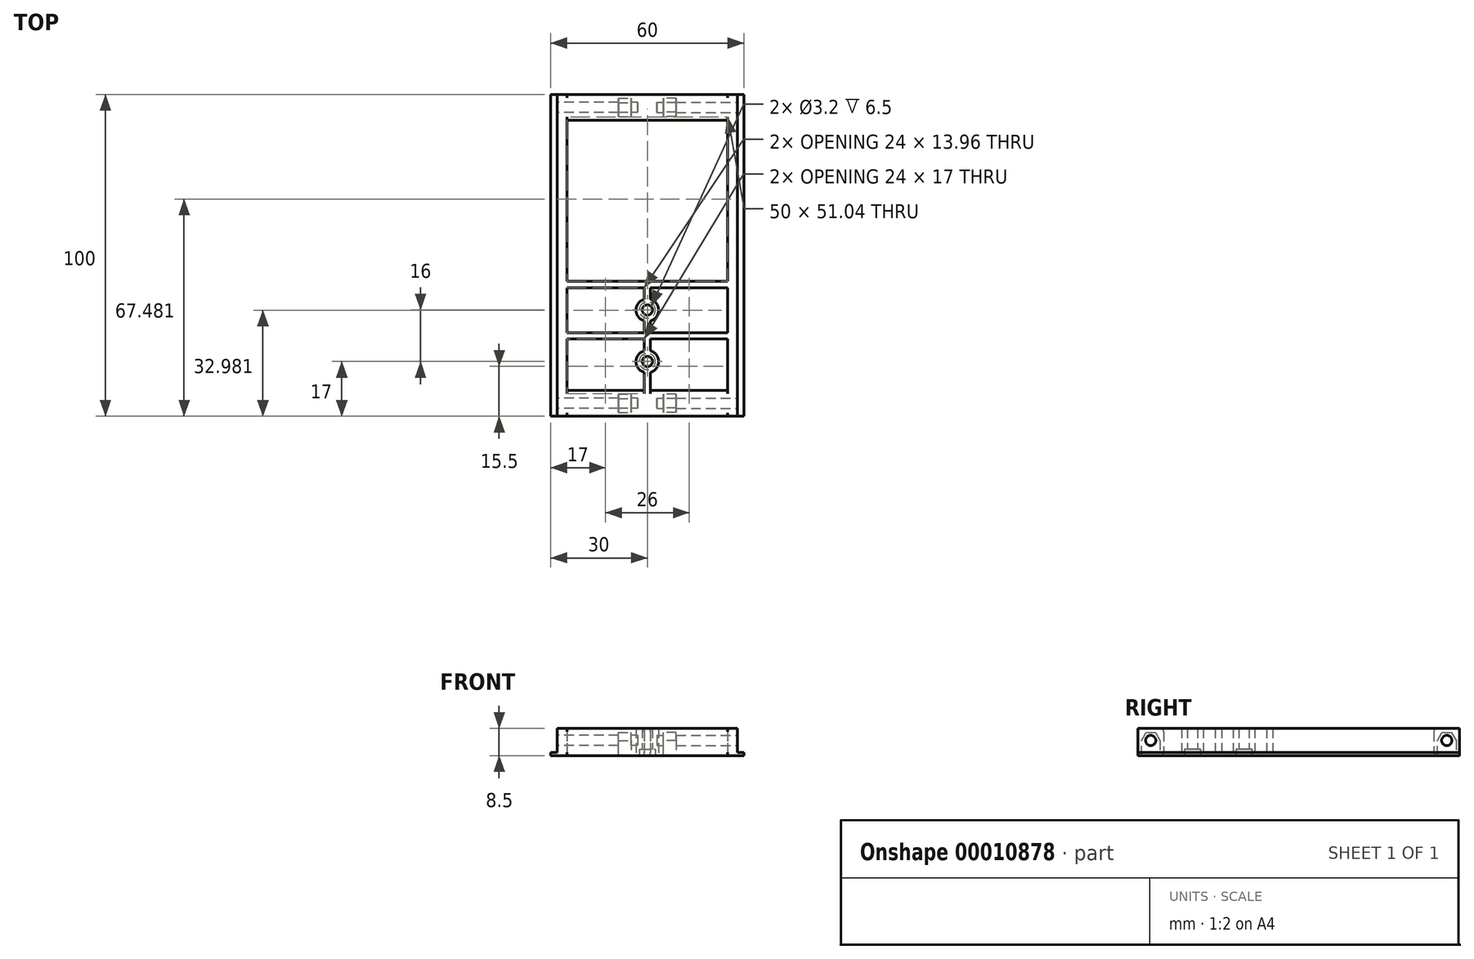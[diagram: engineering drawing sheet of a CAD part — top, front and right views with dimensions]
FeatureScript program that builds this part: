
annotation { "Feature Type Name" : "Feature", "Feature Type Description" : "" }
export const myFeature = defineFeature(function(context is Context, id is Id, definition is map)
    precondition{}
    {
        {
            var Q0;
            Q0=qCreatedBy(makeId("Front.planeOp"),FACE);
            var sketch = newSketch(context, id + "F0", { "sketchPlane" : qUnion([Q0])});
            skLineSegment(sketch, "E0.bottom", {"start": v(0, 0) * mm, "end": v(5, 0) * mm});
            skLineSegment(sketch, "E0.top", {"start": v(0, 1) * mm, "end": v(2, 1) * mm});
            skLineSegment(sketch, "E0.left", {"start": v(0, 0) * mm, "end": v(0, 1) * mm});
            skLineSegment(sketch, "E0.right", {"start": v(5, 0) * mm, "end": v(5, 1) * mm});
            skLineSegment(sketch, "E1.bottom", {"start": v(5, 1) * mm, "end": v(2, 1) * mm, "construction": true});
            skLineSegment(sketch, "E1.top", {"start": v(5, 8.5) * mm, "end": v(2, 8.5) * mm});
            skLineSegment(sketch, "E1.left", {"start": v(5, 1) * mm, "end": v(5, 8.5) * mm});
            skLineSegment(sketch, "E1.right", {"start": v(2, 1) * mm, "end": v(2, 8.5) * mm});
            skSolve(sketch);
        }
        {
            var Q0;
            Q0 = qSketchRegion(id + "F0", true);
            extrude(context, id + "F1", {"entities" : qUnion([Q0]), "depth" : 100 * mm});
        }
        {
            var Q0;
            Q0=makeQuery(id+"F1.opExtrude","SWEPT_FACE",FACE,{"disambiguationData":[OSD([sQuery(id+"F0.wireOp",EDGE,"E1.right")])]});
            var sketch = newSketch(context, id + "F2", { "sketchPlane" : qUnion([Q0])});
            skLineSegment(sketch, "E2", {"start": v(4, 4.75) * mm, "end": v(50, 4.75) * mm, "construction": true});
            skLineSegment(sketch, "E3", {"start": v(50, 4.75) * mm, "end": v(96, 4.75) * mm, "construction": true});
            skCircle(sketch, "E4", {"center": v(4, 4.75) * mm, "radius": 1.6 * mm});
            skCircle(sketch, "E5", {"center": v(96, 4.75) * mm, "radius": 1.6 * mm});
            skLineSegment(sketch, "E6", {"start": v(50, 4.75) * mm, "end": v(50, 1) * mm, "construction": true});
            skLineSegment(sketch, "E7", {"start": v(4, 4.75) * mm, "end": v(0, 4.75) * mm, "construction": true});
            skPoint(sketch, "E8", {"position": v(0, 1) * mm});
            skSolve(sketch);
        }
        {
            var Q0;
            Q0=makeQuery(id+"F1.opExtrude","SWEPT_FACE",FACE,{"disambiguationData":[OSD([sQuery(id+"F0.wireOp",EDGE,"E0.right"),sQuery(id+"F0.wireOp",EDGE,"E1.left")])]});
            var sketch = newSketch(context, id + "F3", { "sketchPlane" : qUnion([Q0])});
            skLineSegment(sketch, "E9.bottom", {"start": v(-99, 8.5) * mm, "end": v(-93, 8.5) * mm});
            skLineSegment(sketch, "E9.top", {"start": v(-99, 0) * mm, "end": v(-93, 0) * mm});
            skLineSegment(sketch, "E9.left", {"start": v(-100, 7.5) * mm, "end": v(-100, 1) * mm});
            skLineSegment(sketch, "E9.right", {"start": v(-92, 7.5) * mm, "end": v(-92, 1) * mm});
            skLineSegment(sketch, "E10.bottom", {"start": v(-7, 8.5) * mm, "end": v(-1, 8.5) * mm});
            skLineSegment(sketch, "E10.top", {"start": v(-7, 0) * mm, "end": v(-1, 0) * mm});
            skLineSegment(sketch, "E10.left", {"start": v(-8, 7.5) * mm, "end": v(-8, 1) * mm});
            skLineSegment(sketch, "E10.right", {"start": v(0, 7.5) * mm, "end": v(0, 1) * mm});
            skPoint(sketch, "E11.visualSharp", {"position": v(-100, 0) * mm});
            skArc(sketch, "E11.filletArc", {"start": v(-100, 1) * mm, "mid": v(-99.7, 0.3) * mm, "end": v(-99, 0) * mm});
            skPoint(sketch, "E12.visualSharp", {"position": v(-100, 8.5) * mm});
            skArc(sketch, "E12.filletArc", {"start": v(-99, 8.5) * mm, "mid": v(-99.7, 8.2) * mm, "end": v(-100, 7.5) * mm});
            skPoint(sketch, "E13.visualSharp", {"position": v(-92, 8.5) * mm});
            skArc(sketch, "E13.filletArc", {"start": v(-92, 7.5) * mm, "mid": v(-92.3, 8.2) * mm, "end": v(-93, 8.5) * mm});
            skPoint(sketch, "E14.visualSharp", {"position": v(-92, 0) * mm});
            skArc(sketch, "E14.filletArc", {"start": v(-93, 0) * mm, "mid": v(-92.3, 0.3) * mm, "end": v(-92, 1) * mm});
            skPoint(sketch, "E15.visualSharp", {"position": v(-8, 8.5) * mm});
            skArc(sketch, "E15.filletArc", {"start": v(-7, 8.5) * mm, "mid": v(-7.7, 8.2) * mm, "end": v(-8, 7.5) * mm});
            skPoint(sketch, "E16.visualSharp", {"position": v(0, 8.5) * mm});
            skArc(sketch, "E16.filletArc", {"start": v(0, 7.5) * mm, "mid": v(-0.3, 8.2) * mm, "end": v(-1, 8.5) * mm});
            skPoint(sketch, "E17.visualSharp", {"position": v(0, 0) * mm});
            skArc(sketch, "E17.filletArc", {"start": v(-1, 0) * mm, "mid": v(-0.3, 0.3) * mm, "end": v(0, 1) * mm});
            skPoint(sketch, "E18.visualSharp", {"position": v(-8, 0) * mm});
            skArc(sketch, "E18.filletArc", {"start": v(-8, 1) * mm, "mid": v(-7.7, 0.3) * mm, "end": v(-7, 0) * mm});
            skLineSegment(sketch, "E19", {"start": v(-100, 7.5) * mm, "end": v(-92, 7.5) * mm, "construction": true});
            skLineSegment(sketch, "E20", {"start": v(-8, 7.5) * mm, "end": v(0, 7.5) * mm, "construction": true});
            skSolve(sketch);
        }
        {
            var Q0;
            Q0 = qSketchRegion(id + "F3", true);
            extrude(context, id + "F4", {"entities" : qUnion([Q0]), "operationType" : NewBodyOperationType.ADD, "depth" : 25 * mm});
        }
        {
            var Q0;
            Q0 = qSketchRegion(id + "F2", true);
            extrude(context, id + "F5", {"entities" : qUnion([Q0]), "operationType" : NewBodyOperationType.REMOVE, "oppositeDirection" : true, "depth" : 25 * mm});
        }
        {
            var Q0;
            Q0=qCreatedBy(makeId("Right.planeOp"),FACE);
            cPlane(context, id + "F6", {"entities" : qUnion([Q0]), "cplaneType" : CPlaneType.OFFSET, "offset" : 25 * mm, "width" : 150 * mm, "height" : 150 * mm});
        }
        {
            var Q0;
            Q0=qCreatedBy(id+"F6.planeOp",FACE);
            var sketch = newSketch(context, id + "F7", { "sketchPlane" : qUnion([Q0])});
            skLineSegment(sketch, "E21", {"start": v(-4, 4.75) * mm, "end": v(-96, 4.75) * mm, "construction": true});
            skCircle(sketch, "E22.cCircle", {"center": v(-4, 4.75) * mm, "radius": 2.5 * mm, "construction": true});
            skLineSegment(sketch, "E22.0", {"start": v(-2.56, 2.25) * mm, "end": v(-5.44, 2.25) * mm, "construction": true});
            skLineSegment(sketch, "E22.1", {"start": v(-5.44, 2.25) * mm, "end": v(-6.89, 4.75) * mm, "construction": true});
            skLineSegment(sketch, "E22.2", {"start": v(-6.89, 4.75) * mm, "end": v(-5.44, 7.25) * mm});
            skLineSegment(sketch, "E22.3", {"start": v(-5.44, 7.25) * mm, "end": v(-2.56, 7.25) * mm});
            skLineSegment(sketch, "E22.4", {"start": v(-2.56, 7.25) * mm, "end": v(-1.11, 4.75) * mm});
            skLineSegment(sketch, "E22.5", {"start": v(-1.11, 4.75) * mm, "end": v(-2.56, 2.25) * mm, "construction": true});
            skPoint(sketch, "E22.0.midPoint", {"position": v(-4, 2.25) * mm});
            skCircle(sketch, "E23.cCircle", {"center": v(-96, 4.75) * mm, "radius": 2.5 * mm, "construction": true});
            skLineSegment(sketch, "E23.0", {"start": v(-94.56, 2.25) * mm, "end": v(-97.44, 2.25) * mm, "construction": true});
            skLineSegment(sketch, "E23.1", {"start": v(-97.44, 2.25) * mm, "end": v(-98.89, 4.75) * mm, "construction": true});
            skLineSegment(sketch, "E23.2", {"start": v(-98.89, 4.75) * mm, "end": v(-97.44, 7.25) * mm});
            skLineSegment(sketch, "E23.3", {"start": v(-97.44, 7.25) * mm, "end": v(-94.56, 7.25) * mm});
            skLineSegment(sketch, "E23.4", {"start": v(-94.56, 7.25) * mm, "end": v(-93.11, 4.75) * mm});
            skLineSegment(sketch, "E23.5", {"start": v(-93.11, 4.75) * mm, "end": v(-94.56, 2.25) * mm, "construction": true});
            skPoint(sketch, "E23.0.midPoint", {"position": v(-96, 2.25) * mm});
            skLineSegment(sketch, "E24", {"start": v(-1.11, 4.75) * mm, "end": v(-1.11, 0) * mm});
            skLineSegment(sketch, "E25", {"start": v(-1.11, 0) * mm, "end": v(-6.89, 0) * mm});
            skLineSegment(sketch, "E26", {"start": v(-6.89, 0) * mm, "end": v(-6.89, 4.75) * mm});
            skLineSegment(sketch, "E27", {"start": v(-93.11, 4.75) * mm, "end": v(-93.11, 0) * mm});
            skLineSegment(sketch, "E28", {"start": v(-93.11, 0) * mm, "end": v(-98.89, 0) * mm});
            skLineSegment(sketch, "E29", {"start": v(-98.89, 0) * mm, "end": v(-98.89, 4.75) * mm});
            skSolve(sketch);
        }
        {
            var Q0;
            Q0 = qSketchRegion(id + "F7", true);
            extrude(context, id + "F8", {"entities" : qUnion([Q0]), "operationType" : NewBodyOperationType.REMOVE, "oppositeDirection" : true, "depth" : 4 * mm});
        }
        {
            var Q0;
            Q0=makeQuery(id+"F1.opExtrude","SWEPT_BODY",BODY,{"disambiguationData":[OSD([sQuery(id+"F0.wireOp",EDGE,"E0.bottom"),sQuery(id+"F0.wireOp",EDGE,"E0.top"),sQuery(id+"F0.wireOp",EDGE,"E0.left"),sQuery(id+"F0.wireOp",EDGE,"E0.right"),sQuery(id+"F0.wireOp",EDGE,"E1.top"),sQuery(id+"F0.wireOp",EDGE,"E1.left"),sQuery(id+"F0.wireOp",EDGE,"E1.right")])]});
            var Q1;
            Q1=makeQuery(id+"F4.opExtrude","CAP_FACE",FACE,{"disambiguationData":[OSD([sQuery(id+"F3.wireOp",EDGE,"E9.bottom"),sQuery(id+"F3.wireOp",EDGE,"E9.top"),sQuery(id+"F3.wireOp",EDGE,"E9.left"),sQuery(id+"F3.wireOp",EDGE,"E9.right"),sQuery(id+"F3.wireOp",EDGE,"E11.filletArc"),sQuery(id+"F3.wireOp",EDGE,"E12.filletArc"),sQuery(id+"F3.wireOp",EDGE,"E13.filletArc"),sQuery(id+"F3.wireOp",EDGE,"E14.filletArc")])],"isStart":false});
            mirror(context, id + "F9", {"operationType" : NewBodyOperationType.ADD, "entities" : qUnion([Q0]), "mirrorPlane" : qUnion([Q1])});
        }
        {
            var Q0;
            Q0=qCreatedBy(makeId("Top.planeOp"),FACE);
            var sketch = newSketch(context, id + "F10", { "sketchPlane" : qUnion([Q0])});
            skLineSegment(sketch, "E30.bottom", {"start": v(55, -58.04) * mm, "end": v(5, -58.04) * mm});
            skLineSegment(sketch, "E30.top", {"start": v(55, -60.04) * mm, "end": v(31, -60.04) * mm});
            skLineSegment(sketch, "E30.left", {"start": v(55, -58.04) * mm, "end": v(55, -60.04) * mm});
            skLineSegment(sketch, "E30.right", {"start": v(5, -58.04) * mm, "end": v(5, -60.04) * mm});
            skLineSegment(sketch, "E31.bottom", {"start": v(31, -60.04) * mm, "end": v(29, -60.04) * mm, "construction": true});
            skLineSegment(sketch, "E31.top", {"start": v(31, -93) * mm, "end": v(29, -93) * mm});
            skLineSegment(sketch, "E31.left", {"start": v(29, -60.04) * mm, "end": v(29, -63.65) * mm});
            skLineSegment(sketch, "E31.right", {"start": v(31, -60.04) * mm, "end": v(31, -63.65) * mm});
            skPoint(sketch, "E32", {"position": v(30, -60.04) * mm});
            skLineSegment(sketch, "E33", {"start": v(30, -60.04) * mm, "end": v(30, -67) * mm, "construction": true});
            skLineSegment(sketch, "E34", {"start": v(30, -67) * mm, "end": v(30, -83) * mm, "construction": true});
            skCircle(sketch, "E35", {"center": v(30, -67) * mm, "radius": 1.6 * mm});
            skCircle(sketch, "E36", {"center": v(30, -83) * mm, "radius": 1.6 * mm});
            skLineSegment(sketch, "E37.trimOffspring", {"start": v(29, -60.04) * mm, "end": v(5, -60.04) * mm});
            skArc(sketch, "E38", {"start": v(29, -79.65) * mm, "mid": v(26.5, -83) * mm, "end": v(29, -86.35) * mm});
            skArc(sketch, "E39", {"start": v(31, -70.35) * mm, "mid": v(33.5, -67) * mm, "end": v(31, -63.65) * mm});
            skLineSegment(sketch, "E40.trimOffspring", {"start": v(31, -86.35) * mm, "end": v(31, -93) * mm});
            skLineSegment(sketch, "E41.trimOffspring", {"start": v(29, -86.35) * mm, "end": v(29, -93) * mm});
            skArc(sketch, "E42.trimOffspring", {"start": v(31, -86.35) * mm, "mid": v(33.5, -83) * mm, "end": v(31, -79.65) * mm});
            skArc(sketch, "E43.trimOffspring", {"start": v(29, -63.65) * mm, "mid": v(26.5, -67) * mm, "end": v(29, -70.35) * mm});
            skLineSegment(sketch, "E44.trimOffspring", {"start": v(31, -70.35) * mm, "end": v(31, -75) * mm});
            skLineSegment(sketch, "E45.trimOffspring", {"start": v(29, -70.35) * mm, "end": v(29, -75) * mm});
            skPoint(sketch, "E46", {"position": v(29, -75) * mm});
            skLineSegment(sketch, "E47.trimOffspring", {"start": v(29, -75) * mm, "end": v(29, -79.65) * mm});
            skPoint(sketch, "E48", {"position": v(31, -75) * mm});
            skLineSegment(sketch, "E49.trimOffspring", {"start": v(31, -75) * mm, "end": v(31, -79.65) * mm});
            skLineSegment(sketch, "E50", {"start": v(60, -100) * mm, "end": v(60, 0) * mm, "construction": true});
            skLineSegment(sketch, "E51", {"start": v(60, -50) * mm, "end": v(0, -50) * mm, "construction": true});
            skLineSegment(sketch, "E52.bottom", {"start": v(29, -76) * mm, "end": v(5, -76) * mm});
            skLineSegment(sketch, "E52.top", {"start": v(29, -74) * mm, "end": v(5, -74) * mm});
            skLineSegment(sketch, "E52.left", {"start": v(29, -76) * mm, "end": v(29, -74) * mm});
            skLineSegment(sketch, "E52.right", {"start": v(5, -76) * mm, "end": v(5, -74) * mm});
            skLineSegment(sketch, "E53.bottom", {"start": v(31, -76) * mm, "end": v(55, -76) * mm});
            skLineSegment(sketch, "E53.top", {"start": v(31, -74) * mm, "end": v(55, -74) * mm});
            skLineSegment(sketch, "E53.left", {"start": v(31, -76) * mm, "end": v(31, -74) * mm});
            skLineSegment(sketch, "E53.right", {"start": v(55, -76) * mm, "end": v(55, -74) * mm});
            skSolve(sketch);
        }
        {
            var Q0;
            Q0 = qSketchRegion(id + "F10", true);
            extrude(context, id + "F11", {"entities" : qUnion([Q0]), "operationType" : NewBodyOperationType.ADD, "depth" : 8.5 * mm});
        }
        {
            var Q0;
            {var subQ0=makeQuery(id+"F4.boolean.opBoolean","MERGE",FACE,{"derivedFrom":[makeQuery(id+"F1.opExtrude","SWEPT_FACE",FACE,{"disambiguationData":[OSD([sQuery(id+"F0.wireOp",EDGE,"E0.bottom")])]}),makeQuery(id+"F4.opExtrude","SWEPT_FACE",FACE,{"disambiguationData":[OSD([sQuery(id+"F3.wireOp",EDGE,"E9.top")])]}),makeQuery(id+"F4.opExtrude","SWEPT_FACE",FACE,{"disambiguationData":[OSD([sQuery(id+"F3.wireOp",EDGE,"E10.top")])]})]});Q0=makeQuery(id+"F11.boolean.opBoolean","MERGE",FACE,{"derivedFrom":[makeQuery(id+"F9.boolean.opBoolean","MERGE",FACE,{"derivedFrom":[subQ0,makeQuery(id+"F9.opPattern","COPY",FACE,{"derivedFrom":subQ0,"instanceName":"1"})]}),makeQuery(id+"F11.opExtrude","CAP_FACE",FACE,{"disambiguationData":[OSD([sQuery(id+"F10.wireOp",EDGE,"E30.bottom"),sQuery(id+"F10.wireOp",EDGE,"E30.top"),sQuery(id+"F10.wireOp",EDGE,"E30.left"),sQuery(id+"F10.wireOp",EDGE,"E30.right"),sQuery(id+"F10.wireOp",EDGE,"E31.top"),sQuery(id+"F10.wireOp",EDGE,"E31.left"),sQuery(id+"F10.wireOp",EDGE,"E31.right"),sQuery(id+"F10.wireOp",EDGE,"E35"),sQuery(id+"F10.wireOp",EDGE,"E36"),sQuery(id+"F10.wireOp",EDGE,"E37.trimOffspring"),sQuery(id+"F10.wireOp",EDGE,"E38"),sQuery(id+"F10.wireOp",EDGE,"E39"),sQuery(id+"F10.wireOp",EDGE,"E40.trimOffspring"),sQuery(id+"F10.wireOp",EDGE,"E41.trimOffspring"),sQuery(id+"F10.wireOp",EDGE,"E42.trimOffspring"),sQuery(id+"F10.wireOp",EDGE,"E43.trimOffspring"),sQuery(id+"F10.wireOp",EDGE,"E44.trimOffspring"),sQuery(id+"F10.wireOp",EDGE,"E45.trimOffspring")])],"isStart":true})]});}
            var sketch = newSketch(context, id + "F12", { "sketchPlane" : qUnion([Q0])});
            skCircle(sketch, "E54", {"center": v(30, 83) * mm, "radius": 2.5 * mm});
            skCircle(sketch, "E55", {"center": v(30, 67) * mm, "radius": 2.5 * mm});
            skSolve(sketch);
        }
        {
            var Q0;
            Q0 = qSketchRegion(id + "F12", true);
            extrude(context, id + "F13", {"entities" : qUnion([Q0]), "operationType" : NewBodyOperationType.REMOVE, "oppositeDirection" : true, "depth" : 2 * mm});
        }
    });
